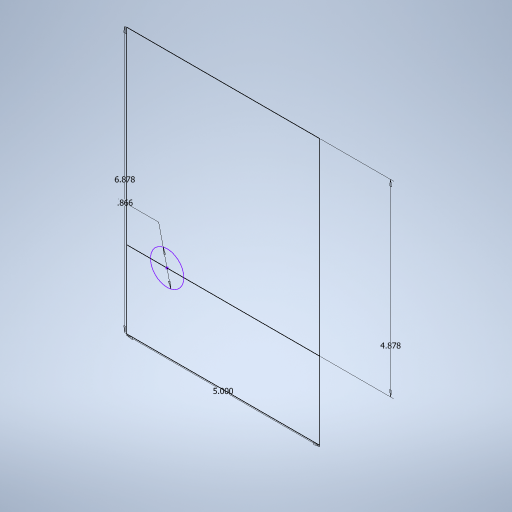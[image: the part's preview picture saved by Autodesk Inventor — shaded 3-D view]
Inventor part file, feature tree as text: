
AUTODESK INVENTOR PART (.ipt)
format: ipt  version: 2023 (Build 270158000, 158)  size: 237,056 bytes
history: native  units: in
note: dims shown in document units (in); Inventor stores cm internally (conversion verified against a paired STEP export)
features: sketch x1
ambient origin geometry x8: Origin, YZ Plane, XZ Plane, XY Plane, X Axis, Y Axis, Z Axis, Center Point
feature tree (1):
  sketch  "Sketch1"  dims[d0=5.0in d1=6.878in d2=4.878in d3=0.866in]
